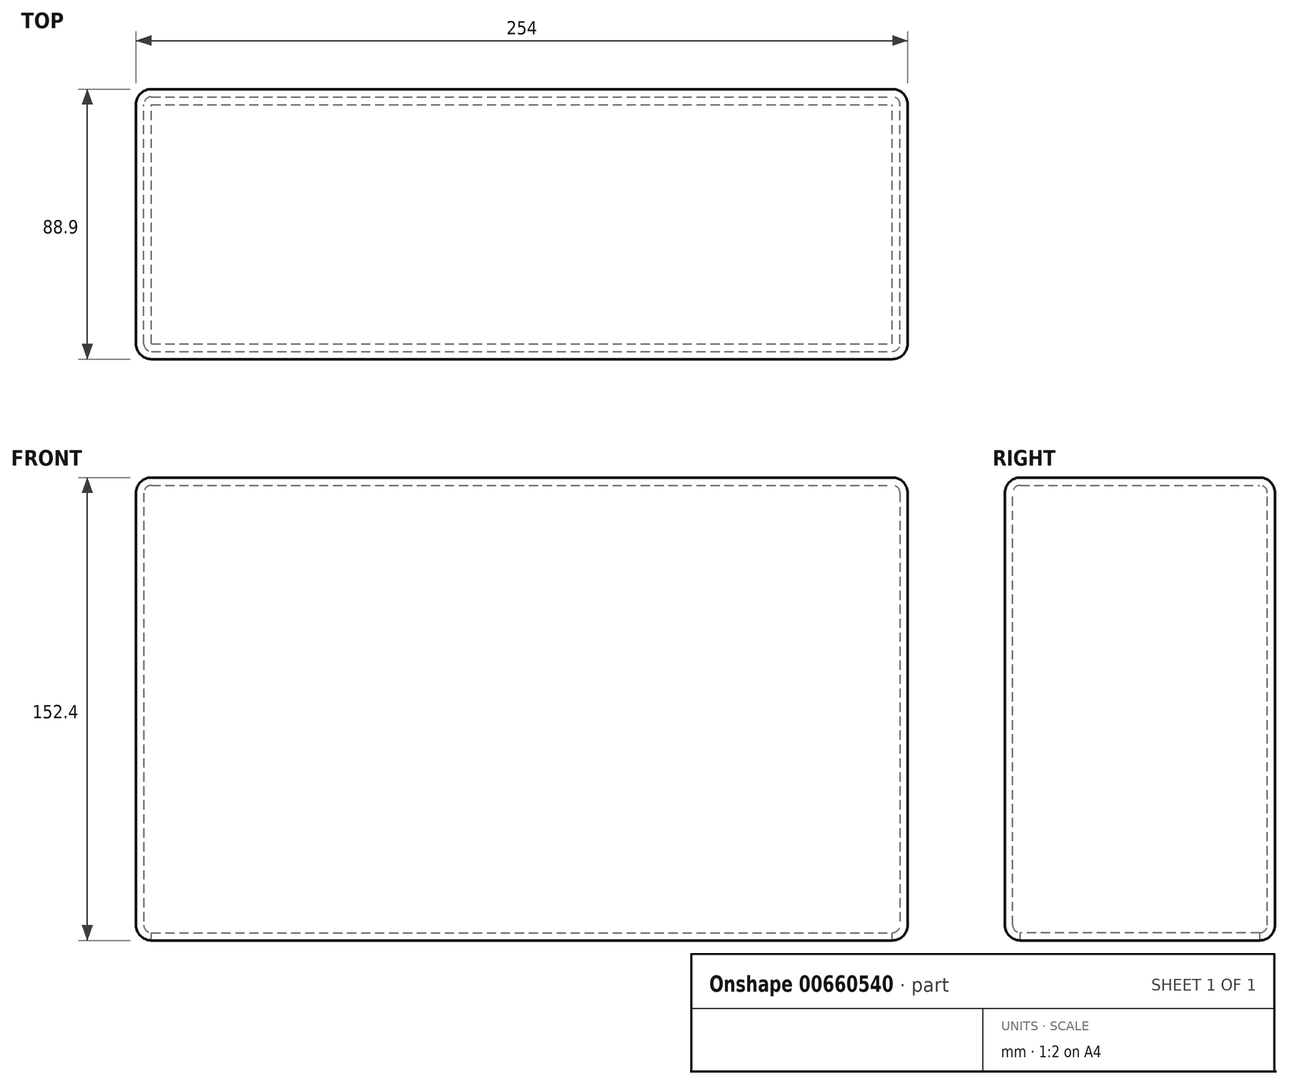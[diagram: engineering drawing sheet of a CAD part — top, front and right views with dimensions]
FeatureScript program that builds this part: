
annotation { "Feature Type Name" : "Feature", "Feature Type Description" : "" }
export const myFeature = defineFeature(function(context is Context, id is Id, definition is map)
    precondition{}
    {
        {
            var Q0;
            Q0=qCreatedBy(makeId("Front.planeOp"),FACE);
            var sketch = newSketch(context, id + "F0", { "sketchPlane" : qUnion([Q0])});
            skLineSegment(sketch, "E0.bottom", {"start": v(-132.4, 75.09) * mm, "end": v(121.6, 75.09) * mm});
            skLineSegment(sketch, "E0.top", {"start": v(-132.4, -77.31) * mm, "end": v(121.6, -77.31) * mm});
            skLineSegment(sketch, "E0.left", {"start": v(-132.4, 75.09) * mm, "end": v(-132.4, -77.31) * mm});
            skLineSegment(sketch, "E0.right", {"start": v(121.6, 75.09) * mm, "end": v(121.6, -77.31) * mm});
            skSolve(sketch);
        }
        {
            var Q0;
            Q0 = qSketchRegion(id + "F0", true);
            extrude(context, id + "F1", {"entities" : qUnion([Q0]), "depth" : 88.9 * mm, "offsetDistance" : 25.4 * mm});
        }
        {
            var Q0;
            Q0=makeQuery(id+"F1.opExtrude","CAP_EDGE",EDGE,{"disambiguationData":[OSD([sQuery(id+"F0.wireOp",EDGE,"E0.right")])],"isStart":false});
            var Q1;
            Q1=makeQuery(id+"F1.opExtrude","CAP_EDGE",EDGE,{"disambiguationData":[OSD([sQuery(id+"F0.wireOp",EDGE,"E0.right")])],"isStart":true});
            fillet(context, id + "F2", {"entities" : qUnion([Q0, Q1]), "radius" : 5.08 * mm, "tangentPropagation" : true, "allowEdgeOverflow" : false});
        }
        {
            var Q0;
            Q0=makeQuery(id+"F1.opExtrude","CAP_EDGE",EDGE,{"disambiguationData":[OSD([sQuery(id+"F0.wireOp",EDGE,"E0.bottom")])],"isStart":false});
            var Q1;
            Q1=makeQuery(id+"F1.opExtrude","CAP_EDGE",EDGE,{"disambiguationData":[OSD([sQuery(id+"F0.wireOp",EDGE,"E0.top")])],"isStart":false});
            fillet(context, id + "F3", {"entities" : qUnion([Q0, Q1]), "radius" : 5.08 * mm, "tangentPropagation" : true, "allowEdgeOverflow" : false});
        }
        {
            var Q0;
            Q0=makeQuery(id+"F1.opExtrude","CAP_EDGE",EDGE,{"disambiguationData":[OSD([sQuery(id+"F0.wireOp",EDGE,"E0.left")])],"isStart":true});
            var Q1;
            Q1=makeQuery(id+"F1.opExtrude","CAP_EDGE",EDGE,{"disambiguationData":[OSD([sQuery(id+"F0.wireOp",EDGE,"E0.left")])],"isStart":false});
            fillet(context, id + "F4", {"entities" : qUnion([Q0, Q1]), "radius" : 5.08 * mm, "tangentPropagation" : true, "allowEdgeOverflow" : false});
        }
        {
            var Q0;
            Q0=makeQuery(id+"F1.opExtrude","SWEPT_FACE",FACE,{"disambiguationData":[OSD([sQuery(id+"F0.wireOp",EDGE,"E0.top")])]});
            shell(context, id + "F5", {"entities" : qUnion([Q0]), "thickness" : 2.54 * mm});
        }
    });
